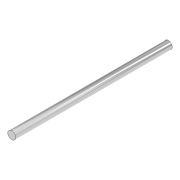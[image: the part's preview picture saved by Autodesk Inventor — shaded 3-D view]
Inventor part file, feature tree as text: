
AUTODESK INVENTOR PART (.ipt)
format: ipt  version: 2020 (Build 240168000, 168)  size: 74,240 bytes
history: native  units: in
note: dims shown in document units (in); Inventor stores cm internally (conversion verified against a paired STEP export)
features: extrude x1, sketch x1
ambient origin geometry x8: Origin, YZ Plane, XZ Plane, XY Plane, X Axis, Y Axis, Z Axis, Center Point
bodies: Solid1 (feature_tree)
feature tree (2):
  extrude  "Extrusion1"  Depth=3.937in TaperAngle=0.0deg
  sketch  "Sketch1"  dims[d0=0.1969in d1=3.937in d2=0.0in]
